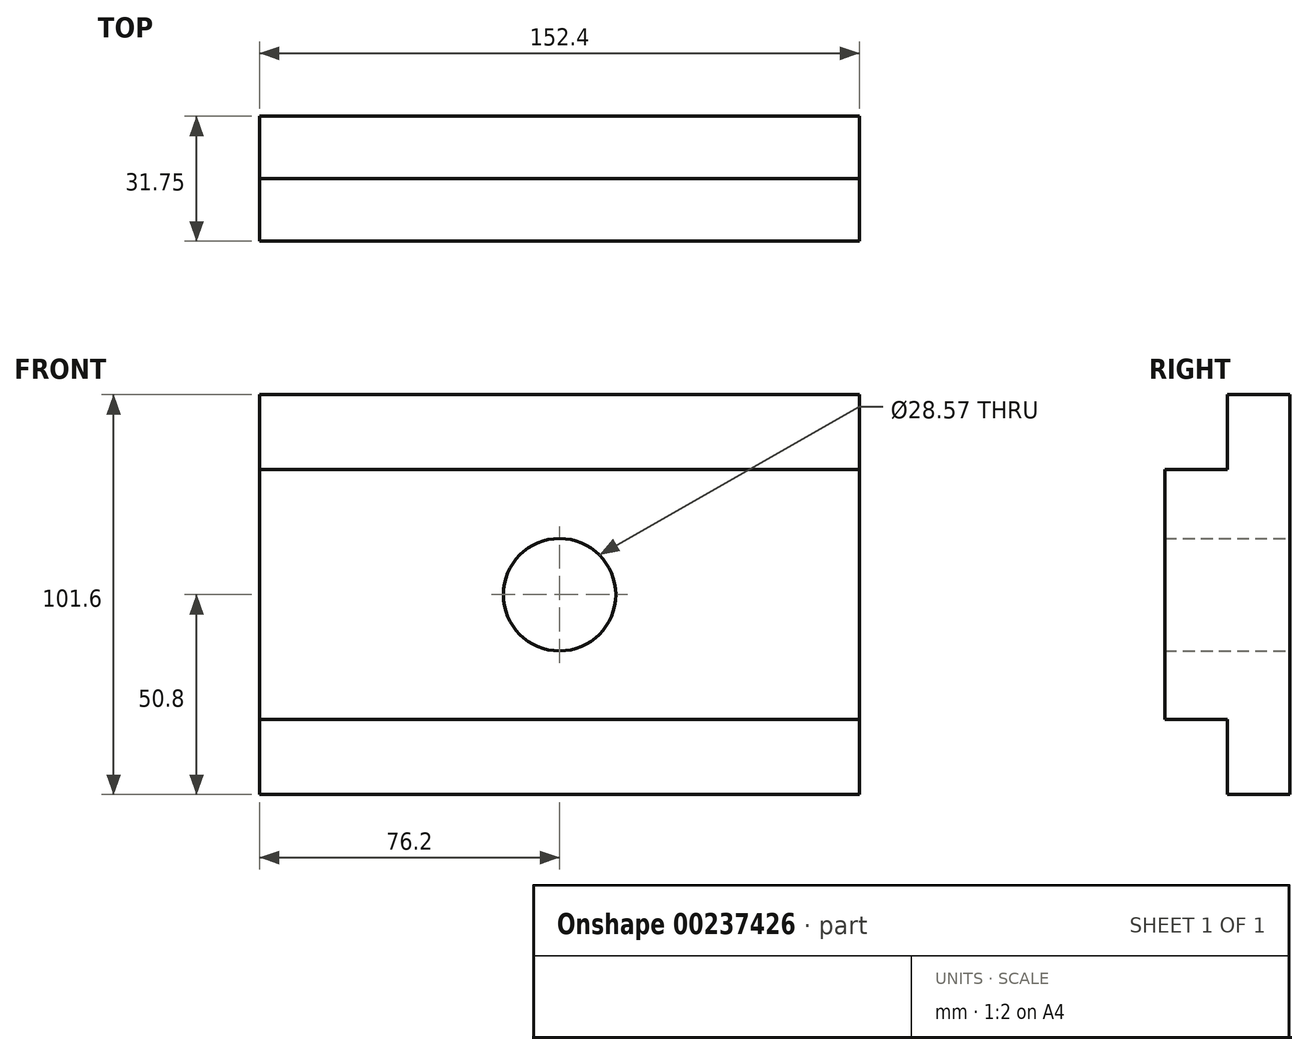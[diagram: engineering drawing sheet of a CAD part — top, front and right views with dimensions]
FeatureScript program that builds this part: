
annotation { "Feature Type Name" : "Feature", "Feature Type Description" : "" }
export const myFeature = defineFeature(function(context is Context, id is Id, definition is map)
    precondition{}
    {
        {
            var Q0;
            Q0=qCreatedBy(makeId("Top.planeOp"),FACE);
            var sketch = newSketch(context, id + "F0", { "sketchPlane" : qUnion([Q0])});
            skLineSegment(sketch, "E0.bottom", {"start": v(76.2, -7.94) * mm, "end": v(-76.2, -7.94) * mm});
            skLineSegment(sketch, "E0.top", {"start": v(76.2, 7.94) * mm, "end": v(-76.2, 7.94) * mm});
            skLineSegment(sketch, "E0.left", {"start": v(76.2, -7.94) * mm, "end": v(76.2, 7.94) * mm});
            skLineSegment(sketch, "E0.right", {"start": v(-76.2, -7.94) * mm, "end": v(-76.2, 7.94) * mm});
            skPoint(sketch, "E0.middle", {"position": v(0, 0) * mm});
            skSolve(sketch);
        }
        {
            var Q0;
            Q0=makeQuery(id+"F0.imprint","IMPRINT",FACE,{"disambiguationData":[TD([[makeQuery(id+"F0.imprint","IMPRINT",EDGE,{"derivedFrom":sQuery(id+"F0.wireOp",EDGE,"E0.bottom")}),-1.0]])]});
            extrude(context, id + "F1", {"entities" : qUnion([Q0]), "depth" : 101.6 * mm});
        }
        {
            var Q0;
            Q0=makeQuery(id+"F1.opExtrude","SWEPT_FACE",FACE,{"disambiguationData":[OSD([sQuery(id+"F0.wireOp",EDGE,"E0.top")])]});
            var sketch = newSketch(context, id + "F2", { "sketchPlane" : qUnion([Q0])});
            skLineSegment(sketch, "E1", {"start": v(-76.2, 19.05) * mm, "end": v(76.2, 19.05) * mm});
            skPoint(sketch, "E1.endSnap0", {"position": v(76.2, 50.8) * mm});
            skLineSegment(sketch, "E2", {"start": v(76.2, 19.05) * mm, "end": v(76.2, 82.55) * mm});
            skLineSegment(sketch, "E3", {"start": v(76.2, 82.55) * mm, "end": v(-76.2, 82.55) * mm});
            skLineSegment(sketch, "E4", {"start": v(-76.2, 82.55) * mm, "end": v(-76.2, 19.05) * mm});
            skPoint(sketch, "E5", {"position": v(0, 50.8) * mm});
            skSolve(sketch);
        }
        {
            var Q0;
            Q0=makeQuery(id+"F2.imprint","IMPRINT",FACE,{"disambiguationData":[TD([[makeQuery(id+"F2.imprint","IMPRINT",EDGE,{"derivedFrom":sQuery(id+"F2.wireOp",EDGE,"E1")}),1.0]])]});
            extrude(context, id + "F3", {"entities" : qUnion([Q0]), "operationType" : NewBodyOperationType.ADD, "oppositeDirection" : true, "depth" : 31.75 * mm});
        }
        {
            var Q0;
            Q0=sQuery(id+"F2.wireOp",VERTEX,"E5");
            var Q1;
            Q1=makeQuery(id+"F1.opExtrude","SWEPT_BODY",BODY,{"disambiguationData":[OSD([sQuery(id+"F0.wireOp",EDGE,"E0.bottom"),sQuery(id+"F0.wireOp",EDGE,"E0.top"),sQuery(id+"F0.wireOp",EDGE,"E0.left"),sQuery(id+"F0.wireOp",EDGE,"E0.right")])]});
            hole(context, id + "F4", {"style" : HoleStyle.SIMPLE, "endStyle" : HoleEndStyle.THROUGH, "holeDiameter" : 28.57 * mm, "locations" : qUnion([Q0]), "scope" : qUnion([Q1]), "isTappedThrough" : true});
        }
    });
